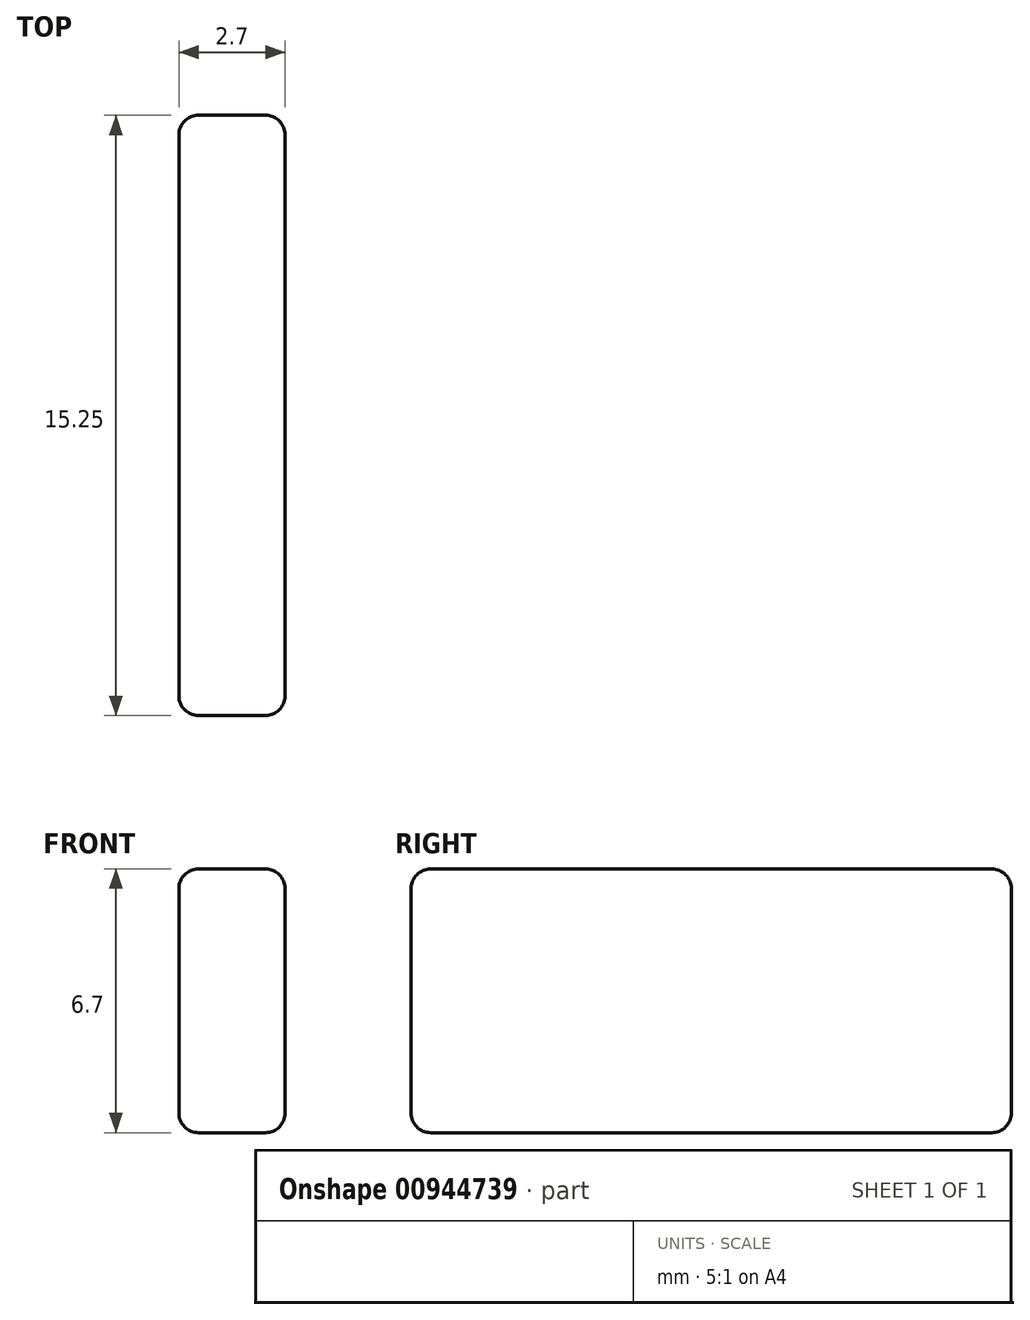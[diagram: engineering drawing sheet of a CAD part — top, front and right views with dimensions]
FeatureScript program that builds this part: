
annotation { "Feature Type Name" : "Feature", "Feature Type Description" : "" }
export const myFeature = defineFeature(function(context is Context, id is Id, definition is map)
    precondition{}
    {
        {
            var Q0;
            Q0=qCreatedBy(makeId("Front.planeOp"),FACE);
            var sketch = newSketch(context, id + "F0", { "sketchPlane" : qUnion([Q0])});
            skLineSegment(sketch, "E0.bottom", {"start": v(1.35, -3.35) * mm, "end": v(-1.35, -3.35) * mm});
            skLineSegment(sketch, "E0.top", {"start": v(1.35, 3.35) * mm, "end": v(-1.35, 3.35) * mm});
            skLineSegment(sketch, "E0.left", {"start": v(1.35, -3.35) * mm, "end": v(1.35, 3.35) * mm});
            skLineSegment(sketch, "E0.right", {"start": v(-1.35, -3.35) * mm, "end": v(-1.35, 3.35) * mm});
            skPoint(sketch, "E0.middle", {"position": v(0, 0) * mm});
            skSolve(sketch);
        }
        {
            var Q0;
            Q0 = qSketchRegion(id + "F0", true);
            extrude(context, id + "F1", {"entities" : qUnion([Q0]), "depth" : 15.25 * mm, "offsetDistance" : 25 * mm});
        }
        {
            var Q0;
            Q0=makeQuery(id+"F1.opExtrude","CAP_EDGE",EDGE,{"disambiguationData":[OSD([sQuery(id+"F0.wireOp",EDGE,"E0.left")])],"isStart":false});
            var Q1;
            Q1=makeQuery(id+"F1.opExtrude","CAP_EDGE",EDGE,{"disambiguationData":[OSD([sQuery(id+"F0.wireOp",EDGE,"E0.right")])],"isStart":false});
            var Q2;
            Q2=makeQuery(id+"F1.opExtrude","CAP_EDGE",EDGE,{"disambiguationData":[OSD([sQuery(id+"F0.wireOp",EDGE,"E0.left")])],"isStart":true});
            var Q3;
            Q3=makeQuery(id+"F1.opExtrude","CAP_EDGE",EDGE,{"disambiguationData":[OSD([sQuery(id+"F0.wireOp",EDGE,"E0.right")])],"isStart":true});
            var Q4;
            Q4=makeQuery(id+"F1.opExtrude","SWEPT_EDGE",EDGE,{"disambiguationData":[OSD([sQuery(id+"F0.wireOp",EDGE,"E0.bottom"),sQuery(id+"F0.wireOp",EDGE,"E0.right")])]});
            var Q5;
            Q5=makeQuery(id+"F1.opExtrude","SWEPT_EDGE",EDGE,{"disambiguationData":[OSD([sQuery(id+"F0.wireOp",EDGE,"E0.bottom"),sQuery(id+"F0.wireOp",EDGE,"E0.left")])]});
            var Q6;
            Q6=makeQuery(id+"F1.opExtrude","SWEPT_EDGE",EDGE,{"disambiguationData":[OSD([sQuery(id+"F0.wireOp",EDGE,"E0.top"),sQuery(id+"F0.wireOp",EDGE,"E0.left")])]});
            var Q7;
            Q7=makeQuery(id+"F1.opExtrude","SWEPT_EDGE",EDGE,{"disambiguationData":[OSD([sQuery(id+"F0.wireOp",EDGE,"E0.top"),sQuery(id+"F0.wireOp",EDGE,"E0.right")])]});
            var Q8;
            Q8=makeQuery(id+"F1.opExtrude","CAP_EDGE",EDGE,{"disambiguationData":[OSD([sQuery(id+"F0.wireOp",EDGE,"E0.bottom")])],"isStart":true});
            var Q9;
            Q9=makeQuery(id+"F1.opExtrude","CAP_EDGE",EDGE,{"disambiguationData":[OSD([sQuery(id+"F0.wireOp",EDGE,"E0.top")])],"isStart":true});
            var Q10;
            Q10=makeQuery(id+"F1.opExtrude","CAP_EDGE",EDGE,{"disambiguationData":[OSD([sQuery(id+"F0.wireOp",EDGE,"E0.top")])],"isStart":false});
            var Q11;
            Q11=makeQuery(id+"F1.opExtrude","CAP_EDGE",EDGE,{"disambiguationData":[OSD([sQuery(id+"F0.wireOp",EDGE,"E0.bottom")])],"isStart":false});
            fillet(context, id + "F2", {"entities" : qUnion([Q0, Q1, Q2, Q3, Q4, Q5, Q6, Q7, Q8, Q9, Q10, Q11]), "radius" : .5 * mm, "tangentPropagation" : true, "allowEdgeOverflow" : false});
        }
    });
